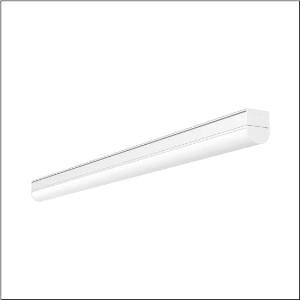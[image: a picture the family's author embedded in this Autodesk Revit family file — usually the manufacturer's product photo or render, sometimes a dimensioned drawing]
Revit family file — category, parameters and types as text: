
# Revit family: ecopack_r__31_51lj12mnm70a_41d1
name_source: partatom
category: Lighting Fixtures
units: mm (PartAtom-declared; Revit-internal decimal feet)

## family parameters
Cut with Voids When Loaded = No
Host = Face
Light Source = No
Part Type = Normal
Room Calculation Point = No
Round Connector Dimension = Use Diameter
Shared = No

## types (1)
- --- (1 x LED, 6780 lm, 50 W, 5000K)
    Apparent Load = 50 VA
    CIE Flux Codes = 39 67 87 89 100
    Color Rendering = 80
    Color Temperature = 5000K
    Default Elevation = 1800 mm
    Description = Ecopack® 31, diffuser luminaire, primary optical cover: cover, of PC, frosted, light emission: direct distribution, primary light characteristic: symmetric, installation type: surface-mounted, LED, rated luminous flux: 7.000lm, luminous efficacy: 140lm/W, light colour: 830/840/850, colour temperature: 3000/4000/5000K, control gear: ON/OFF Multilumen, with terminal, 3-pole, mains connection: 220..240V, AC, 50/60Hz, rated input power: 50W, housing, of aluminium, traffic white (RAL 9016), length: 1.450mm, width: 56mm, height: 68mm, end cap, of PC, white, protection rating (complete): IP20, insulation class (complete): insulation class I (protective earthing), certification: CE, impact resistance: IK06, permissible operating ambient temperature: -20..+40°C, packaging unit: 1 piece
    Height = 68 mm
    Lamp = 1 x LED
    Lamp Light Flux = 6780 lm
    Lamp Power = 50 W
    Lamp count = 1
    Length = 1450 mm
    Luminous efficacy = 136 lm/W
    Manufacturer = Siteco
    ModVariant = No
    Model = 51LJ12MNM70A
    Mounting Place = Ceiling
    Mounting Type = Surface mounted
    Number of Poles = 1
    OnlyDefault = Yes
    Power Factor = 1
    Product Name = Ecopack® 31
    Product group = diffuser luminaire
    ProductGroupID = 306
    Protection Class = Protection class I
    Protection Degree = IP 20
    RLX_Detail_Level = 1
    RLX_Emergency_Light_Flux = 0 lm
    RLX_Emergency_Type = 0
    RLX_Emergency_Type_DB = No
    RlxData = <blob elided: 39049 chars, md5=2324684e>
    Socket = socket
    Standby Power = 0 W
    System Light Flux = 6780 lm
    System Power = 50 W
    Type Comments = individual setting: colour temperature 5000K, luminous flux: 100 % | (ON | ON)
    Type Image = l_1007033.jpg
    URL = http://relux.com
    VarID = @adj_177241
    Voltage = 0 V
    Weight = 0.00 kg
    Width = 56 mm

## geometry (parser evidence)
native form markers: Blend x4, Sweep x14
no freeform markers — native parametric forms only
